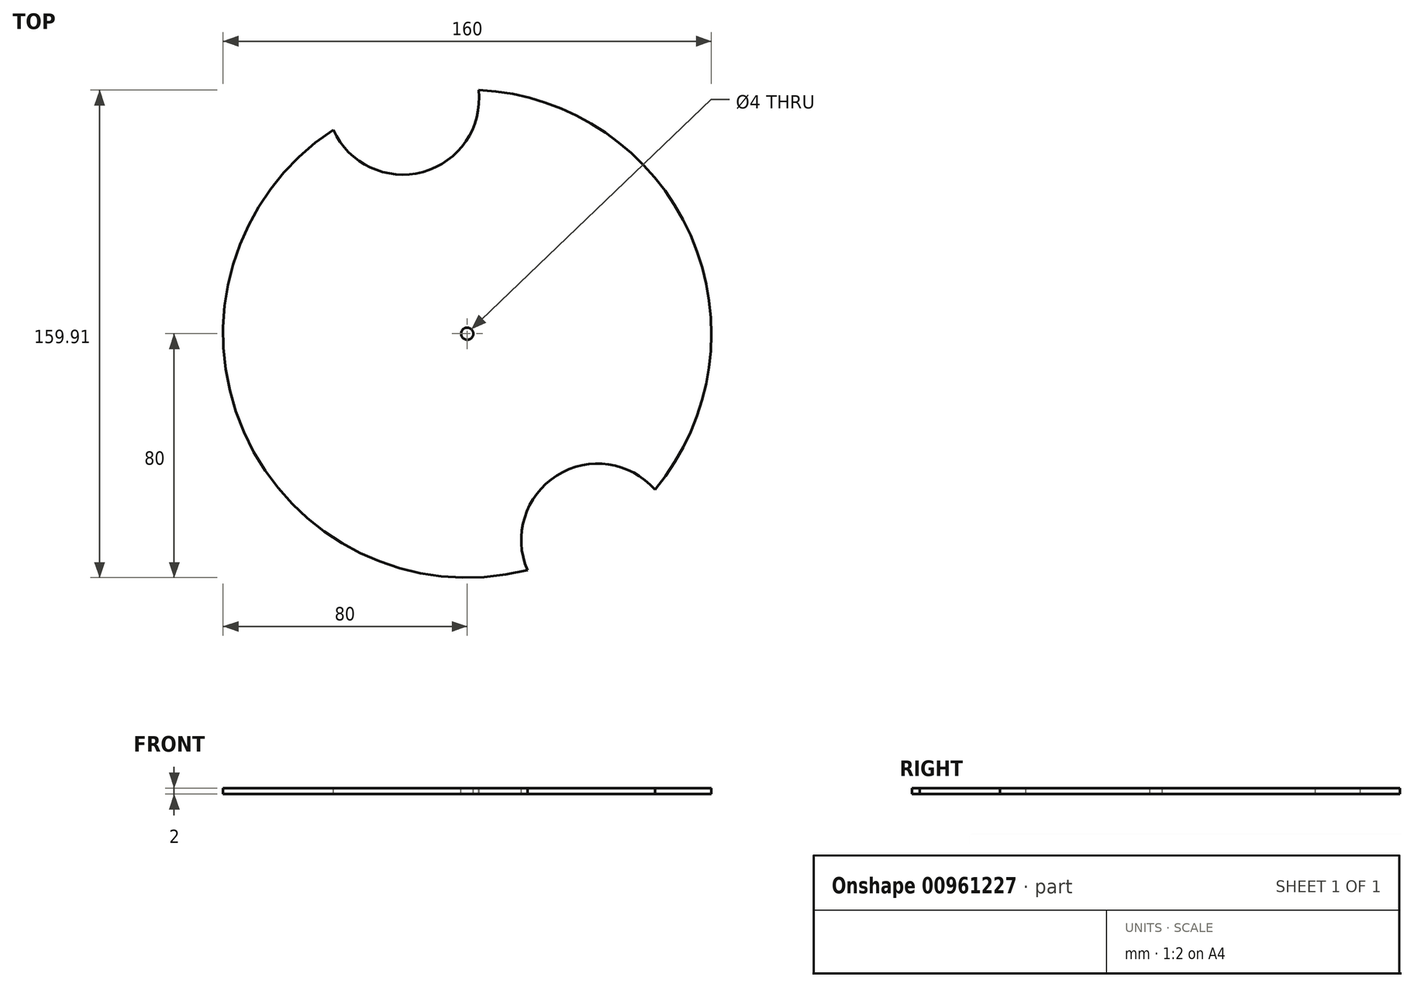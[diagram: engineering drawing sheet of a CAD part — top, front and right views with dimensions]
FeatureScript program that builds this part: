
annotation { "Feature Type Name" : "Feature", "Feature Type Description" : "" }
export const myFeature = defineFeature(function(context is Context, id is Id, definition is map)
    precondition{}
    {
        {
            var Q0;
            Q0=qCreatedBy(makeId("Top.planeOp"),FACE);
            var sketch = newSketch(context, id + "F0", { "sketchPlane" : qUnion([Q0])});
            skCircle(sketch, "E0", {"center": v(0, 0) * mm, "radius": 80 * mm});
            skSolve(sketch);
        }
        {
            var Q0;
            Q0 = qSketchRegion(id + "F0", true);
            extrude(context, id + "F1", {"entities" : qUnion([Q0]), "depth" : 2 * mm, "offsetDistance" : 25.4 * mm});
        }
        {
            var Q0;
            Q0=makeQuery(id+"F1.opExtrude","CAP_FACE",FACE,{"disambiguationData":[OSD([sQuery(id+"F0.wireOp",EDGE,"E0")])],"isStart":false});
            var sketch = newSketch(context, id + "F2", { "sketchPlane" : qUnion([Q0])});
            skCircle(sketch, "E1", {"center": v(42.71, -67.64) * mm, "radius": 25 * mm});
            skSolve(sketch);
        }
        {
            var Q0;
            Q0 = qSketchRegion(id + "F2", true);
            extrude(context, id + "F3", {"entities" : qUnion([Q0]), "operationType" : NewBodyOperationType.REMOVE, "oppositeDirection" : true, "depth" : 25.4 * mm, "offsetDistance" : 25.4 * mm});
        }
        {
            var Q0;
            Q0=makeQuery(id+"F1.opExtrude","CAP_FACE",FACE,{"disambiguationData":[OSD([sQuery(id+"F0.wireOp",EDGE,"E0")])],"isStart":false});
            var sketch = newSketch(context, id + "F4", { "sketchPlane" : qUnion([Q0])});
            skCircle(sketch, "E2", {"center": v(0, 0) * mm, "radius": 2 * mm});
            skSolve(sketch);
        }
        {
            var Q0;
            Q0 = qSketchRegion(id + "F4", true);
            extrude(context, id + "F5", {"entities" : qUnion([Q0]), "operationType" : NewBodyOperationType.REMOVE, "oppositeDirection" : true, "depth" : 25.4 * mm, "offsetDistance" : 25.4 * mm});
        }
        {
            var Q0;
            Q0=makeQuery(id+"F1.opExtrude","CAP_FACE",FACE,{"disambiguationData":[OSD([sQuery(id+"F0.wireOp",EDGE,"E0")])],"isStart":false});
            var sketch = newSketch(context, id + "F6", { "sketchPlane" : qUnion([Q0])});
            skCircle(sketch, "E3", {"center": v(-21.1, 77.17) * mm, "radius": 25 * mm});
            skSolve(sketch);
        }
        {
            var Q0;
            {var subQ0=sQuery(id+"F6.wireOp",EDGE,"E3");var subQ1=makeQuery(id+"F1.opExtrude","CAP_EDGE",EDGE,{"disambiguationData":[OSD([sQuery(id+"F0.wireOp",EDGE,"E0")])],"isStart":false});var subQ2=makeQuery(id+"F6.imprint","INTERSECT",VERTEX,{"disambiguationData":[OD(0.0)],"derivedFrom":[subQ1,subQ0]});Q0=makeQuery(id+"F6.imprint","IMPRINT",FACE,{"disambiguationData":[TD([[makeQuery(id+"F6.imprint","IMPRINT",EDGE,{"disambiguationData":[TD([[subQ2,1.0]])],"derivedFrom":subQ0}),1.0]])]});}
            var Q1;
            {var subQ0=sQuery(id+"F6.wireOp",EDGE,"E3");var subQ1=makeQuery(id+"F1.opExtrude","CAP_EDGE",EDGE,{"disambiguationData":[OSD([sQuery(id+"F0.wireOp",EDGE,"E0")])],"isStart":false});var subQ2=makeQuery(id+"F6.imprint","INTERSECT",VERTEX,{"disambiguationData":[OD(0.0)],"derivedFrom":[subQ1,subQ0]});Q1=makeQuery(id+"F6.imprint","IMPRINT",FACE,{"disambiguationData":[TD([[makeQuery(id+"F6.imprint","IMPRINT",EDGE,{"disambiguationData":[TD([[subQ2,-1.0]])],"derivedFrom":subQ0}),1.0]])]});}
            extrude(context, id + "F7", {"entities" : qUnion([Q0, Q1]), "operationType" : NewBodyOperationType.REMOVE, "oppositeDirection" : true, "depth" : 25.4 * mm, "offsetDistance" : 25.4 * mm});
        }
    });
